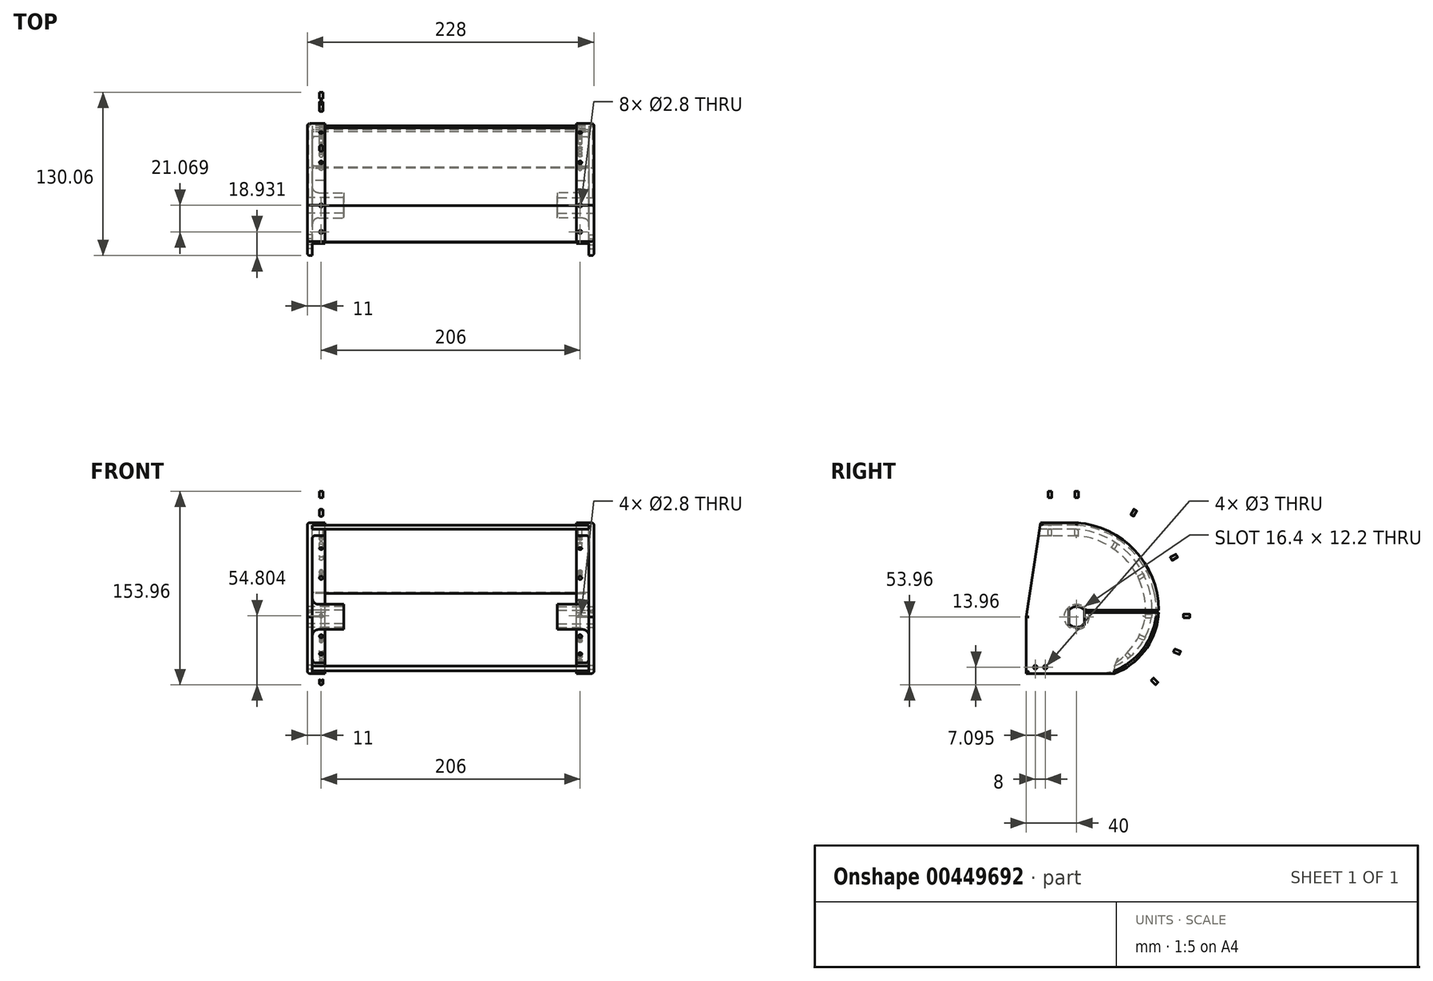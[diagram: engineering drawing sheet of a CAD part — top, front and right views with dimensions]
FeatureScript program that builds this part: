
annotation { "Feature Type Name" : "Feature", "Feature Type Description" : "" }
export const myFeature = defineFeature(function(context is Context, id is Id, definition is map)
    precondition{}
    {
        {
            var Q0;
            Q0=qCreatedBy(makeId("Right.planeOp"),FACE);
            var sketch = newSketch(context, id + "F0", { "sketchPlane" : qUnion([Q0])});
            skCircle(sketch, "E0", {"center": v(0, 0) * mm, "radius": 40 * mm});
            skCircle(sketch, "E1", {"center": v(0, 0) * mm, "radius": 8.2 * mm});
            skLineSegment(sketch, "E2", {"start": v(-6.1, 5.48) * mm, "end": v(-6.1, -5.48) * mm});
            skLineSegment(sketch, "E3", {"start": v(6.1, -5.48) * mm, "end": v(6.1, 5.48) * mm});
            skLineSegment(sketch, "E4", {"start": v(0, 0) * mm, "end": v(0, -45) * mm, "construction": true});
            skLineSegment(sketch, "E5", {"start": v(0, 0) * mm, "end": v(65, 0) * mm, "construction": true});
            skLineSegment(sketch, "E6", {"start": v(0, 0) * mm, "end": v(0, 75) * mm, "construction": true});
            skArc(sketch, "E7", {"start": v(65, 0) * mm, "mid": v(48.17, 51.08) * mm, "end": v(0, 75) * mm});
            skLineSegment(sketch, "E8", {"start": v(0, -45) * mm, "end": v(30, -45) * mm});
            skArc(sketch, "E9", {"start": v(30, -45) * mm, "mid": v(53.79, -27.4) * mm, "end": v(65, 0) * mm});
            skLineSegment(sketch, "E10", {"start": v(0, -45) * mm, "end": v(-40, -45) * mm});
            skLineSegment(sketch, "E11", {"start": v(-40, -45) * mm, "end": v(-40, 0) * mm});
            skLineSegment(sketch, "E12", {"start": v(-28.66, 75) * mm, "end": v(0, 75) * mm});
            skLineSegment(sketch, "E13", {"start": v(-40, 0) * mm, "end": v(-28.66, 75) * mm});
            skLineSegment(sketch, "E14.0", {"start": v(-28.96, 73) * mm, "end": v(-0.07, 73) * mm});
            skArc(sketch, "E14.1", {"start": v(61.76, 19.33) * mm, "mid": v(39.87, 56.56) * mm, "end": v(-0.07, 73) * mm});
            skArc(sketch, "E14.2", {"start": v(29.5, -43.05) * mm, "mid": v(57.45, -17.97) * mm, "end": v(61.76, 19.33) * mm});
            skArc(sketch, "E15.0", {"start": v(20.83, -42.2) * mm, "mid": v(52.6, -19.83) * mm, "end": v(58.54, 18.58) * mm});
            skArc(sketch, "E15.1", {"start": v(58.54, 18.58) * mm, "mid": v(37.77, 54) * mm, "end": v(-0.18, 69.7) * mm});
            skLineSegment(sketch, "E15.2", {"start": v(-29.46, 69.7) * mm, "end": v(-0.18, 69.7) * mm});
            skArc(sketch, "E16.1", {"start": v(54.69, 0.26) * mm, "mid": v(40.66, 44) * mm, "end": v(-0.35, 64.7) * mm});
            skLineSegment(sketch, "E16.2", {"start": v(-30.22, 64.7) * mm, "end": v(-0.35, 64.7) * mm});
            skLineSegment(sketch, "E17", {"start": v(29.5, -43.05) * mm, "end": v(19.71, -45) * mm});
            skLineSegment(sketch, "E18", {"start": v(20.86, -42.37) * mm, "end": v(20.83, -42.2) * mm});
            skArc(sketch, "E19", {"start": v(20.86, -42.37) * mm, "mid": v(43.09, -25.27) * mm, "end": v(54.69, 0.26) * mm});
            skLineSegment(sketch, "E20", {"start": v(30.2, -39.2) * mm, "end": v(31.32, -36.44) * mm});
            skPoint(sketch, "E21", {"position": v(-32.9, -40) * mm});
            skPoint(sketch, "E22", {"position": v(-24.9, -40) * mm});
            skCircle(sketch, "E23", {"center": v(-32.9, -40) * mm, "radius": 1.5 * mm});
            skCircle(sketch, "E24", {"center": v(-24.9, -40) * mm, "radius": 1.5 * mm});
            skSolve(sketch);
        }
        {
            var Q0;
            Q0=makeQuery(id+"F0.imprint","IMPRINT",FACE,{"disambiguationData":[TD([[makeQuery(id+"F0.imprint","IMPRINT",EDGE,{"derivedFrom":sQuery(id+"F0.wireOp",EDGE,"E7")}),1.0]])]});
            var Q1;
            {var subQ4=sQuery(id+"F0.wireOp",EDGE,"E1");var subQ8=sQuery(id+"F0.wireOp",EDGE,"E2");var subQ9=makeQuery(id+"F0.imprint","INTERSECT",VERTEX,{"disambiguationData":[OD(0.0)],"derivedFrom":[subQ4,subQ8]});Q1=makeQuery(id+"F0.imprint","IMPRINT",FACE,{"disambiguationData":[TD([[makeQuery(id+"F0.imprint","IMPRINT",EDGE,{"disambiguationData":[TD([[subQ9,1.0]])],"derivedFrom":subQ4}),-1.0]])]});}
            var Q2;
            {var subQ0=sQuery(id+"F0.wireOp",EDGE,"E2");Q2=makeQuery(id+"F0.imprint","IMPRINT",FACE,{"disambiguationData":[TD([[makeQuery(id+"F0.imprint","IMPRINT",EDGE,{"derivedFrom":subQ0}),-1.0]])]});}
            var Q3;
            {var subQ0=sQuery(id+"F0.wireOp",EDGE,"E3");Q3=makeQuery(id+"F0.imprint","IMPRINT",FACE,{"disambiguationData":[TD([[makeQuery(id+"F0.imprint","IMPRINT",EDGE,{"derivedFrom":subQ0}),-1.0]])]});}
            var Q4;
            {var subQ12=sQuery(id+"F0.wireOp",EDGE,"E10");Q4=makeQuery(id+"F0.imprint","IMPRINT",FACE,{"disambiguationData":[TD([[makeQuery(id+"F0.imprint","IMPRINT",EDGE,{"derivedFrom":subQ12}),-1.0]])]});}
            var Q5;
            {var subQ4=sQuery(id+"F0.wireOp",EDGE,"E15.0");Q5=makeQuery(id+"F0.imprint","IMPRINT",FACE,{"disambiguationData":[TD([[makeQuery(id+"F0.imprint","IMPRINT",EDGE,{"derivedFrom":subQ4}),1.0]])]});}
            var Q6;
            {var subQ4=sQuery(id+"F0.wireOp",EDGE,"E14.0");Q6=makeQuery(id+"F0.imprint","IMPRINT",FACE,{"disambiguationData":[TD([[makeQuery(id+"F0.imprint","IMPRINT",EDGE,{"derivedFrom":subQ4}),-1.0]])]});}
            var Q7;
            {var subQ0=sQuery(id+"F0.wireOp",EDGE,"E18");Q7=makeQuery(id+"F0.imprint","IMPRINT",FACE,{"disambiguationData":[TD([[makeQuery(id+"F0.imprint","IMPRINT",EDGE,{"derivedFrom":subQ0}),1.0]])]});}
            var Q8;
            {var subQ7=sQuery(id+"F0.wireOp",EDGE,"E15.1");Q8=makeQuery(id+"F0.imprint","IMPRINT",FACE,{"disambiguationData":[TD([[makeQuery(id+"F0.imprint","IMPRINT",EDGE,{"derivedFrom":subQ7}),1.0]])]});}
            var Q9;
            {var subQ0=sQuery(id+"F0.wireOp",EDGE,"E18");Q9=makeQuery(id+"F0.imprint","IMPRINT",FACE,{"disambiguationData":[TD([[makeQuery(id+"F0.imprint","IMPRINT",EDGE,{"derivedFrom":subQ0}),-1.0]])]});}
            var Q10;
            Q10=sQuery(id+"F0.wireOp",EDGE,"E12");
            var Q11;
            Q11=sQuery(id+"F0.wireOp",EDGE,"E13");
            var Q12;
            Q12=sQuery(id+"F0.wireOp",EDGE,"E11");
            var Q13;
            Q13=sQuery(id+"F0.wireOp",EDGE,"E10");
            var Q14;
            Q14=sQuery(id+"F0.wireOp",EDGE,"E8");
            var Q15;
            Q15=sQuery(id+"F0.wireOp",EDGE,"E9");
            var Q16;
            Q16=sQuery(id+"F0.wireOp",EDGE,"E7");
            extrude(context, id + "F1", {"entities" : qUnion([Q0, Q1, Q2, Q3, Q4, Q5, Q6, Q7, Q8, Q9]), "surfaceEntities" : qUnion([Q10, Q11, Q12, Q13, Q14, Q15, Q16]), "depth" : 29 * mm});
        }
        {
            var Q0;
            Q0=makeQuery(id+"F1.opExtrude","CAP_FACE",FACE,{"disambiguationData":[OSD([sQuery(id+"F0.wireOp",EDGE,"E1"),sQuery(id+"F0.wireOp",EDGE,"E2"),sQuery(id+"F0.wireOp",EDGE,"E3"),sQuery(id+"F0.wireOp",EDGE,"E7"),sQuery(id+"F0.wireOp",EDGE,"E8"),sQuery(id+"F0.wireOp",EDGE,"E9"),sQuery(id+"F0.wireOp",EDGE,"E10"),sQuery(id+"F0.wireOp",EDGE,"E11"),sQuery(id+"F0.wireOp",EDGE,"E12"),sQuery(id+"F0.wireOp",EDGE,"E13"),sQuery(id+"F0.wireOp",EDGE,"b91848d7-33e1-4d5c-aaae-2f8c404cd7a8"),sQuery(id+"F0.wireOp",EDGE,"291409aa-1abd-44d4-8dab-fd7a7754a467")])],"isStart":false});
            var sketch = newSketch(context, id + "F2", { "sketchPlane" : qUnion([Q0])});
            skCircle(sketch, "E25", {"center": v(0, 0) * mm, "radius": 10 * mm});
            skSolve(sketch);
        }
        {
            var Q0;
            {var subQ1=sQuery(id+"F0.wireOp",EDGE,"E2");Q0=makeQuery(id+"F2.imprint","IMPRINT",FACE,{"disambiguationData":[TD([[makeQuery(id+"F2.imprint","IMPRINT",EDGE,{"derivedFrom":makeQuery(id+"F1.opExtrude","CAP_EDGE",EDGE,{"disambiguationData":[OSD([subQ1])],"isStart":true})}),-1.0]])]});}
            var Q1;
            Q1=makeQuery(id+"F2.imprint","IMPRINT",FACE,{"disambiguationData":[TD([[makeQuery(id+"F2.imprint","IMPRINT",EDGE,{"derivedFrom":sQuery(id+"F2.wireOp",EDGE,"E25")}),-1.0]])]});
            extrude(context, id + "F3", {"entities" : qUnion([Q0, Q1]), "operationType" : NewBodyOperationType.REMOVE, "oppositeDirection" : true, "depth" : 25 * mm});
        }
        {
            var Q0;
            {var subQ7=sQuery(id+"F0.wireOp",EDGE,"E15.1");Q0=makeQuery(id+"F0.imprint","IMPRINT",FACE,{"disambiguationData":[TD([[makeQuery(id+"F0.imprint","IMPRINT",EDGE,{"derivedFrom":subQ7}),1.0]])]});}
            extrude(context, id + "F4", {"entities" : qUnion([Q0]), "operationType" : NewBodyOperationType.ADD, "depth" : 10 * mm});
        }
        {
            var Q0;
            Q0=makeQuery(id+"F0.imprint","IMPRINT",FACE,{"disambiguationData":[TD([[makeQuery(id+"F0.imprint","IMPRINT",EDGE,{"derivedFrom":sQuery(id+"F0.wireOp",EDGE,"E7")}),1.0]])]});
            extrude(context, id + "F5", {"entities" : qUnion([Q0]), "operationType" : NewBodyOperationType.ADD, "depth" : 10 * mm});
        }
        {
            var Q0;
            Q0=makeQuery(id+"F3.boolean.opBoolean","COPY",EDGE,{"derivedFrom":makeQuery(id+"F3.opExtrude","CAP_EDGE",EDGE,{"disambiguationData":[OSD([sQuery(id+"F2.wireOp",EDGE,"E25")])],"isStart":false})});
            fillet(context, id + "F6", {"entities" : qUnion([Q0]), "radius" : 5 * mm, "tangentPropagation" : true, "allowEdgeOverflow" : false});
        }
        {
            var Q0;
            Q0=makeQuery(id+"F3.boolean.opBoolean","COPY",EDGE,{"derivedFrom":makeQuery(id+"F3.opExtrude","CAP_EDGE",EDGE,{"disambiguationData":[OSD([sQuery(id+"F2.wireOp",EDGE,"E25")])],"isStart":true})});
            var Q1;
            Q1=makeQuery(id+"F4.boolean.opBoolean","INTERSECT",EDGE,{"derivedFrom":[makeQuery(id+"F3.boolean.opBoolean","COPY",FACE,{"derivedFrom":makeQuery(id+"F3.opExtrude","CAP_FACE",FACE,{"disambiguationData":[OSD([sQuery(id+"F0.wireOp",EDGE,"E7"),sQuery(id+"F0.wireOp",EDGE,"E8"),sQuery(id+"F0.wireOp",EDGE,"E9"),sQuery(id+"F0.wireOp",EDGE,"E10"),sQuery(id+"F0.wireOp",EDGE,"E11"),sQuery(id+"F0.wireOp",EDGE,"E12"),sQuery(id+"F0.wireOp",EDGE,"E13"),sQuery(id+"F2.wireOp",EDGE,"E25")])],"isStart":false})}),makeQuery(id+"F4.opExtrude","SWEPT_FACE",FACE,{"disambiguationData":[OSD([sQuery(id+"F0.wireOp",EDGE,"E19")])]})]});
            var Q2;
            Q2=makeQuery(id+"F4.boolean.opBoolean","INTERSECT",EDGE,{"derivedFrom":[makeQuery(id+"F3.boolean.opBoolean","COPY",FACE,{"derivedFrom":makeQuery(id+"F3.opExtrude","CAP_FACE",FACE,{"disambiguationData":[OSD([sQuery(id+"F0.wireOp",EDGE,"E7"),sQuery(id+"F0.wireOp",EDGE,"E8"),sQuery(id+"F0.wireOp",EDGE,"E9"),sQuery(id+"F0.wireOp",EDGE,"E10"),sQuery(id+"F0.wireOp",EDGE,"E11"),sQuery(id+"F0.wireOp",EDGE,"E12"),sQuery(id+"F0.wireOp",EDGE,"E13"),sQuery(id+"F2.wireOp",EDGE,"E25")])],"isStart":false})}),makeQuery(id+"F4.opExtrude","SWEPT_FACE",FACE,{"disambiguationData":[OSD([sQuery(id+"F0.wireOp",EDGE,"E16.1")])]})]});
            var Q3;
            Q3=makeQuery(id+"F4.boolean.opBoolean","INTERSECT",EDGE,{"derivedFrom":[makeQuery(id+"F3.boolean.opBoolean","COPY",FACE,{"derivedFrom":makeQuery(id+"F3.opExtrude","CAP_FACE",FACE,{"disambiguationData":[OSD([sQuery(id+"F0.wireOp",EDGE,"E7"),sQuery(id+"F0.wireOp",EDGE,"E8"),sQuery(id+"F0.wireOp",EDGE,"E9"),sQuery(id+"F0.wireOp",EDGE,"E10"),sQuery(id+"F0.wireOp",EDGE,"E11"),sQuery(id+"F0.wireOp",EDGE,"E12"),sQuery(id+"F0.wireOp",EDGE,"E13"),sQuery(id+"F2.wireOp",EDGE,"E25")])],"isStart":false})}),makeQuery(id+"F4.opExtrude","SWEPT_FACE",FACE,{"disambiguationData":[OSD([sQuery(id+"F0.wireOp",EDGE,"E16.2")])]})]});
            var Q4;
            {var subQ0=sQuery(id+"F0.wireOp",EDGE,"E13");var subQ1=sQuery(id+"F0.wireOp",EDGE,"E11");Q4=makeQuery(id+"F4.boolean.opBoolean","SPLIT",EDGE,{"disambiguationData":[TD([makeQuery(id+"F1.opExtrude","SWEPT_FACE",FACE,{"disambiguationData":[OSD([subQ1])]})])],"derivedFrom":makeQuery(id+"F3.boolean.opBoolean","COPY",EDGE,{"derivedFrom":makeQuery(id+"F3.opExtrude","CAP_EDGE",EDGE,{"disambiguationData":[OSD([subQ0])],"isStart":false})})});}
            var Q5;
            Q5=makeQuery(id+"F3.boolean.opBoolean","COPY",EDGE,{"derivedFrom":makeQuery(id+"F3.opExtrude","CAP_EDGE",EDGE,{"disambiguationData":[OSD([sQuery(id+"F0.wireOp",EDGE,"E11")])],"isStart":false})});
            var Q6;
            Q6=makeQuery(id+"F3.boolean.opBoolean","COPY",EDGE,{"derivedFrom":makeQuery(id+"F3.opExtrude","CAP_EDGE",EDGE,{"disambiguationData":[OSD([sQuery(id+"F0.wireOp",EDGE,"E8"),sQuery(id+"F0.wireOp",EDGE,"E10")])],"isStart":false})});
            var Q7;
            Q7=makeQuery(id+"F1.opExtrude","CAP_EDGE",EDGE,{"disambiguationData":[OSD([sQuery(id+"F0.wireOp",EDGE,"E11")])],"isStart":true});
            var Q8;
            Q8=makeQuery(id+"F1.opExtrude","CAP_EDGE",EDGE,{"disambiguationData":[OSD([sQuery(id+"F0.wireOp",EDGE,"E13")])],"isStart":true});
            var Q9;
            Q9=makeQuery(id+"F1.opExtrude","CAP_EDGE",EDGE,{"disambiguationData":[OSD([sQuery(id+"F0.wireOp",EDGE,"E8"),sQuery(id+"F0.wireOp",EDGE,"E10")])],"isStart":true});
            var Q10;
            Q10=makeQuery(id+"F1.opExtrude","CAP_EDGE",EDGE,{"disambiguationData":[OSD([sQuery(id+"F0.wireOp",EDGE,"E9")])],"isStart":true});
            var Q11;
            Q11=makeQuery(id+"F1.opExtrude","CAP_EDGE",EDGE,{"disambiguationData":[OSD([sQuery(id+"F0.wireOp",EDGE,"E7")])],"isStart":true});
            fillet(context, id + "F7", {"entities" : qUnion([Q0, Q1, Q2, Q3, Q4, Q5, Q6, Q7, Q8, Q9, Q10, Q11]), "radius" : 2 * mm, "tangentPropagation" : true, "allowEdgeOverflow" : false});
        }
        {
            var Q0;
            Q0=makeQuery(id+"F4.opExtrude","CAP_FACE",FACE,{"disambiguationData":[OSD([sQuery(id+"F0.wireOp",EDGE,"E13"),sQuery(id+"F0.wireOp",EDGE,"E15.0"),sQuery(id+"F0.wireOp",EDGE,"E15.1"),sQuery(id+"F0.wireOp",EDGE,"E15.2"),sQuery(id+"F0.wireOp",EDGE,"E16.1"),sQuery(id+"F0.wireOp",EDGE,"E16.2"),sQuery(id+"F0.wireOp",EDGE,"E19"),sQuery(id+"F0.wireOp",EDGE,"E20")])],"isStart":false});
            var Q1;
            Q1=makeQuery(id+"F5.opExtrude","CAP_FACE",FACE,{"disambiguationData":[OSD([sQuery(id+"F0.wireOp",EDGE,"E7"),sQuery(id+"F0.wireOp",EDGE,"E8"),sQuery(id+"F0.wireOp",EDGE,"E9"),sQuery(id+"F0.wireOp",EDGE,"E12"),sQuery(id+"F0.wireOp",EDGE,"E13"),sQuery(id+"F0.wireOp",EDGE,"E14.0"),sQuery(id+"F0.wireOp",EDGE,"E14.1"),sQuery(id+"F0.wireOp",EDGE,"E14.2"),sQuery(id+"F0.wireOp",EDGE,"E17")])],"isStart":false});
            extrude(context, id + "F8", {"entities" : qUnion([Q0, Q1]), "operationType" : NewBodyOperationType.ADD, "depth" : 4 * mm});
        }
        {
            var Q0;
            {var subQ0=sQuery(id+"F0.wireOp",EDGE,"E12");Q0=makeQuery(id+"F8.boolean.opBoolean","MERGE",FACE,{"derivedFrom":[makeQuery(id+"F5.boolean.opBoolean","MERGE",FACE,{"derivedFrom":[makeQuery(id+"F1.opExtrude","SWEPT_FACE",FACE,{"disambiguationData":[OSD([subQ0])]}),makeQuery(id+"F5.opExtrude","SWEPT_FACE",FACE,{"disambiguationData":[OSD([subQ0])]})]}),makeQuery(id+"F8.opExtrude","SWEPT_FACE",FACE,{"disambiguationData":[OSD([subQ0])]})]});}
            var sketch = newSketch(context, id + "F9", { "sketchPlane" : qUnion([Q0])});
            skCircle(sketch, "E26", {"center": v(11, 0) * mm, "radius": 1.4 * mm});
            skCircle(sketch, "E27", {"center": v(11, -21.07) * mm, "radius": 1.4 * mm});
            skSolve(sketch);
        }
        {
            var Q0;
            Q0=makeQuery(id+"F9.imprint","IMPRINT",FACE,{"disambiguationData":[TD([[makeQuery(id+"F9.imprint","IMPRINT",EDGE,{"derivedFrom":sQuery(id+"F9.wireOp",EDGE,"E27")}),-1.0]])]});
            cPlane(context, id + "F10", {"entities" : qUnion([Q0]), "cplaneType" : CPlaneType.OFFSET, "offset" : 20 * mm, "width" : 150 * mm, "height" : 150 * mm});
        }
        {
            var Q0;
            Q0=qCreatedBy(id+"F10.planeOp",FACE);
            var sketch = newSketch(context, id + "F11", { "sketchPlane" : qUnion([Q0])});
            skCircle(sketch, "E28.0", {"center": v(11, 0) * mm, "radius": 1.4 * mm});
            skCircle(sketch, "E29.0", {"center": v(11, -21.07) * mm, "radius": 1.4 * mm});
            skSolve(sketch);
        }
        {
            var Q0;
            Q0=makeQuery(id+"F11.imprint","IMPRINT",FACE,{"disambiguationData":[TD([[makeQuery(id+"F11.imprint","IMPRINT",EDGE,{"derivedFrom":sQuery(id+"F11.wireOp",EDGE,"E28.0")}),1.0]])]});
            var Q1;
            Q1=makeQuery(id+"F11.imprint","IMPRINT",FACE,{"disambiguationData":[TD([[makeQuery(id+"F11.imprint","IMPRINT",EDGE,{"derivedFrom":sQuery(id+"F11.wireOp",EDGE,"E29.0")}),1.0]])]});
            extrude(context, id + "F12", {"entities" : qUnion([Q0, Q1]), "depth" : 5 * mm});
        }
        {
            var Q0;
            Q0=makeQuery(id+"F12.opExtrude","SWEPT_BODY",BODY,{"disambiguationData":[OSD([sQuery(id+"F11.wireOp",EDGE,"E28.0")])]});
            var Q1;
            {var subQ0=sQuery(id+"F0.wireOp",EDGE,"E7");Q1=makeQuery(id+"F8.boolean.opBoolean","MERGE",FACE,{"derivedFrom":[makeQuery(id+"F5.boolean.opBoolean","MERGE",FACE,{"derivedFrom":[makeQuery(id+"F1.opExtrude","SWEPT_FACE",FACE,{"disambiguationData":[OSD([subQ0])]}),makeQuery(id+"F5.opExtrude","SWEPT_FACE",FACE,{"disambiguationData":[OSD([subQ0])]})]}),makeQuery(id+"F8.opExtrude","SWEPT_FACE",FACE,{"disambiguationData":[OSD([subQ0])]})]});}
            circularPattern(context, id + "F13", {"entities" : qUnion([Q0]), "axis" : qUnion([Q1]), "angle" : 30 * degree, "instanceCount" : round(4)});
        }
        {
            var Q0;
            Q0=makeQuery(id+"F13.opPattern","COPY",BODY,{"derivedFrom":makeQuery(id+"F12.opExtrude","SWEPT_BODY",BODY,{"disambiguationData":[OSD([sQuery(id+"F11.wireOp",EDGE,"E28.0")])]}),"instanceName":"3"});
            var Q1;
            {var subQ0=sQuery(id+"F0.wireOp",EDGE,"E9");Q1=makeQuery(id+"F5.boolean.opBoolean","MERGE",FACE,{"derivedFrom":[makeQuery(id+"F1.opExtrude","SWEPT_FACE",FACE,{"disambiguationData":[OSD([subQ0])]}),makeQuery(id+"F5.opExtrude","SWEPT_FACE",FACE,{"disambiguationData":[OSD([subQ0])]})]});}
            circularPattern(context, id + "F14", {"entities" : qUnion([Q0]), "axis" : qUnion([Q1]), "angle" : 22 * degree, "instanceCount" : round(3)});
        }
        {
            var Q0;
            Q0=makeQuery(id+"F12.opExtrude","CAP_FACE",FACE,{"disambiguationData":[OSD([sQuery(id+"F11.wireOp",EDGE,"E29.0")])],"isStart":true});
            var Q1;
            Q1=makeQuery(id+"F12.opExtrude","CAP_FACE",FACE,{"disambiguationData":[OSD([sQuery(id+"F11.wireOp",EDGE,"E28.0")])],"isStart":true});
            extrude(context, id + "F15", {"entities" : qUnion([Q0, Q1]), "operationType" : NewBodyOperationType.REMOVE, "depth" : 40 * mm});
        }
        {
            var Q0;
            Q0=makeQuery(id+"F13.opPattern","COPY",FACE,{"derivedFrom":makeQuery(id+"F12.opExtrude","CAP_FACE",FACE,{"disambiguationData":[OSD([sQuery(id+"F11.wireOp",EDGE,"E28.0")])],"isStart":true}),"instanceName":"1"});
            extrude(context, id + "F16", {"entities" : qUnion([Q0]), "operationType" : NewBodyOperationType.REMOVE, "depth" : 40 * mm});
        }
        {
            var Q0;
            Q0=makeQuery(id+"F13.opPattern","COPY",FACE,{"derivedFrom":makeQuery(id+"F12.opExtrude","CAP_FACE",FACE,{"disambiguationData":[OSD([sQuery(id+"F11.wireOp",EDGE,"E28.0")])],"isStart":true}),"instanceName":"2"});
            extrude(context, id + "F17", {"entities" : qUnion([Q0]), "operationType" : NewBodyOperationType.REMOVE, "depth" : 40 * mm});
        }
        {
            var Q0;
            Q0=makeQuery(id+"F13.opPattern","COPY",FACE,{"derivedFrom":makeQuery(id+"F12.opExtrude","CAP_FACE",FACE,{"disambiguationData":[OSD([sQuery(id+"F11.wireOp",EDGE,"E28.0")])],"isStart":true}),"instanceName":"3"});
            extrude(context, id + "F18", {"entities" : qUnion([Q0]), "operationType" : NewBodyOperationType.REMOVE, "depth" : 40 * mm});
        }
        {
            var Q0;
            Q0=makeQuery(id+"F14.opPattern","COPY",FACE,{"derivedFrom":makeQuery(id+"F13.opPattern","COPY",FACE,{"derivedFrom":makeQuery(id+"F12.opExtrude","CAP_FACE",FACE,{"disambiguationData":[OSD([sQuery(id+"F11.wireOp",EDGE,"E28.0")])],"isStart":true}),"instanceName":"3"}),"instanceName":"1"});
            extrude(context, id + "F19", {"entities" : qUnion([Q0]), "operationType" : NewBodyOperationType.REMOVE, "depth" : 40 * mm});
        }
        {
            var Q0;
            Q0=makeQuery(id+"F14.opPattern","COPY",FACE,{"derivedFrom":makeQuery(id+"F13.opPattern","COPY",FACE,{"derivedFrom":makeQuery(id+"F12.opExtrude","CAP_FACE",FACE,{"disambiguationData":[OSD([sQuery(id+"F11.wireOp",EDGE,"E28.0")])],"isStart":true}),"instanceName":"3"}),"instanceName":"2"});
            extrude(context, id + "F20", {"entities" : qUnion([Q0]), "operationType" : NewBodyOperationType.REMOVE, "depth" : 40 * mm});
        }
        {
            var Q0;
            Q0=makeQuery(id+"F1.opExtrude","CAP_EDGE",EDGE,{"disambiguationData":[OSD([sQuery(id+"F0.wireOp",EDGE,"E3")])],"isStart":true});
            var Q1;
            {var subQ0=sQuery(id+"F0.wireOp",EDGE,"E1");Q1=makeQuery(id+"F1.opExtrude","CAP_EDGE",EDGE,{"disambiguationData":[OSD([subQ0]),TDD([makeQuery(id+"F0.imprint","IMPRINT",EDGE,{"disambiguationData":[TD([[makeQuery(id+"F0.imprint","INTERSECT",VERTEX,{"disambiguationData":[OD(0.0)],"derivedFrom":[subQ0,sQuery(id+"F0.wireOp",EDGE,"E2")]}),1.0]])],"derivedFrom":subQ0})])],"isStart":true});}
            var Q2;
            Q2=makeQuery(id+"F1.opExtrude","CAP_EDGE",EDGE,{"disambiguationData":[OSD([sQuery(id+"F0.wireOp",EDGE,"E2")])],"isStart":true});
            var Q3;
            {var subQ0=sQuery(id+"F0.wireOp",EDGE,"E1");Q3=makeQuery(id+"F1.opExtrude","CAP_EDGE",EDGE,{"disambiguationData":[OSD([subQ0]),TDD([makeQuery(id+"F0.imprint","IMPRINT",EDGE,{"disambiguationData":[TD([[makeQuery(id+"F0.imprint","INTERSECT",VERTEX,{"disambiguationData":[OD(1.0)],"derivedFrom":[subQ0,sQuery(id+"F0.wireOp",EDGE,"E2")]}),-1.0]])],"derivedFrom":subQ0})])],"isStart":true});}
            fillet(context, id + "F21", {"entities" : qUnion([Q0, Q1, Q2, Q3]), "radius" : 1 * mm, "tangentPropagation" : true, "allowEdgeOverflow" : false});
        }
        {
            var Q0;
            Q0=makeQuery(id+"F1.opExtrude","CAP_FACE",FACE,{"disambiguationData":[OSD([sQuery(id+"F0.wireOp",EDGE,"E1"),sQuery(id+"F0.wireOp",EDGE,"E2"),sQuery(id+"F0.wireOp",EDGE,"E3"),sQuery(id+"F0.wireOp",EDGE,"E7"),sQuery(id+"F0.wireOp",EDGE,"E8"),sQuery(id+"F0.wireOp",EDGE,"E9"),sQuery(id+"F0.wireOp",EDGE,"E10"),sQuery(id+"F0.wireOp",EDGE,"E11"),sQuery(id+"F0.wireOp",EDGE,"E12"),sQuery(id+"F0.wireOp",EDGE,"E13"),sQuery(id+"F0.wireOp",EDGE,"E23"),sQuery(id+"F0.wireOp",EDGE,"E24")])],"isStart":true});
            var sketch = newSketch(context, id + "F22", { "sketchPlane" : qUnion([Q0])});
            skCircle(sketch, "E30", {"center": v(-65.2, 4.44) * mm, "radius": 1 * mm});
            skArc(sketch, "E31.0", {"start": v(-30, -45) * mm, "mid": v(-53.79, -27.4) * mm, "end": v(-65, 0) * mm});
            skArc(sketch, "E32.0", {"start": v(-65, 0) * mm, "mid": v(-48.17, 51.08) * mm, "end": v(0, 75) * mm});
            skLineSegment(sketch, "E33", {"start": v(-65.2, 4.44) * mm, "end": v(-3.8, 4.44) * mm});
            skCircle(sketch, "E34", {"center": v(-65.2, 4.44) * mm, "radius": 1.5 * mm});
            skLineSegment(sketch, "E35", {"start": v(-65.6, 5.36) * mm, "end": v(-65.84, 5.81) * mm});
            skSolve(sketch);
        }
        {
            var Q0;
            {var subQ0=sQuery(id+"F22.wireOp",EDGE,"E33");var subQ1=sQuery(id+"F22.wireOp",EDGE,"E30");var subQ2=makeQuery(id+"F22.imprint","INTERSECT",VERTEX,{"derivedFrom":[subQ1,subQ0]});Q0=makeQuery(id+"F22.imprint","IMPRINT",FACE,{"disambiguationData":[TD([[makeQuery(id+"F22.imprint","IMPRINT",EDGE,{"disambiguationData":[TD([[subQ2,1.0]])],"derivedFrom":subQ1}),1.0]])]});}
            var Q1;
            {var subQ0=sQuery(id+"F22.wireOp",EDGE,"E32.0");var subQ1=sQuery(id+"F22.wireOp",EDGE,"E30");var subQ2=makeQuery(id+"F22.imprint","INTERSECT",VERTEX,{"disambiguationData":[OD(0.0)],"derivedFrom":[subQ1,subQ0]});Q1=makeQuery(id+"F22.imprint","IMPRINT",FACE,{"disambiguationData":[TD([[makeQuery(id+"F22.imprint","IMPRINT",EDGE,{"disambiguationData":[TD([[subQ2,1.0]])],"derivedFrom":subQ1}),1.0]])]});}
            extrude(context, id + "F23", {"entities" : qUnion([Q0, Q1]), "operationType" : NewBodyOperationType.REMOVE, "oppositeDirection" : true, "depth" : 25 * mm});
        }
        {
            var Q0;
            Q0=qCreatedBy(makeId("Front.planeOp"),FACE);
            cPlane(context, id + "F24", {"entities" : qUnion([Q0]), "cplaneType" : CPlaneType.OFFSET, "offset" : 65 * mm, "oppositeDirection" : true, "width" : 150 * mm, "height" : 150 * mm});
        }
        {
            var Q0;
            Q0=qCreatedBy(id+"F24.planeOp",FACE);
            var sketch = newSketch(context, id + "F25", { "sketchPlane" : qUnion([Q0])});
            skFitSpline(sketch, "E36.0", {"points": [v(2, 3.44) * mm, v(1.7, 3.44) * mm, v(1.48, 3.45) * mm, v(1.36, 3.45) * mm, v(1.25, 3.46) * mm, v(1.15, 3.47) * mm, v(1.07, 3.48) * mm, v(0.96, 3.5) * mm, v(0.87, 3.51) * mm, v(0.8, 3.54) * mm, v(0.7, 3.57) * mm, v(0.61, 3.62) * mm, v(0.54, 3.68) * mm, v(0.47, 3.75) * mm, v(0.4, 3.83) * mm, v(0.36, 3.93) * mm, v(0.33, 4) * mm, v(0.3, 4.09) * mm, v(0.3, 4.18) * mm, v(0.28, 4.27) * mm, v(0.27, 4.36) * mm, v(0.27, 4.45) * mm, v(0.27, 4.57) * mm, v(0.28, 4.67) * mm, v(0.3, 4.77) * mm, v(0.32, 4.88) * mm, v(0.35, 4.97) * mm, v(0.4, 5.05) * mm, v(0.44, 5.13) * mm, v(0.5, 5.2) * mm, v(0.57, 5.24) * mm, v(0.63, 5.3) * mm, v(0.7, 5.33) * mm, v(0.8, 5.36) * mm, v(0.87, 5.39) * mm, v(0.96, 5.4) * mm, v(1.06, 5.42) * mm, v(1.15, 5.43) * mm, v(1.24, 5.44) * mm, v(1.36, 5.44) * mm, v(1.44, 5.44) * mm, v(1.55, 5.44) * mm, v(1.68, 5.44) * mm, v(1.71, 5.44) * mm, v(1.82, 5.44) * mm, v(2, 5.44) * mm]});
            skLineSegment(sketch, "E37.0", {"start": v(0, 0.2) * mm, "end": v(0, 73) * mm});
            skLineSegment(sketch, "E38", {"start": v(0.27, 4.45) * mm, "end": v(0, 4.45) * mm});
            skCircle(sketch, "E39", {"center": v(0, 4.45) * mm, "radius": 1 * mm});
            skSolve(sketch);
        }
        {
            var Q0;
            {var subQ0=sQuery(id+"F25.wireOp",EDGE,"E38");Q0=makeQuery(id+"F25.imprint","IMPRINT",FACE,{"disambiguationData":[TD([[makeQuery(id+"F25.imprint","IMPRINT",EDGE,{"derivedFrom":subQ0}),1.0]])]});}
            var Q1;
            {var subQ0=sQuery(id+"F25.wireOp",EDGE,"E36.0");var subQ3=makeQuery(id+"F25.imprint","INTERSECT",VERTEX,{"derivedFrom":[subQ0,sQuery(id+"F25.wireOp",EDGE,"E38")]});Q1=makeQuery(id+"F25.imprint","IMPRINT",FACE,{"disambiguationData":[TD([[makeQuery(id+"F25.imprint","IMPRINT",EDGE,{"disambiguationData":[TD([[subQ3,1.0]])],"derivedFrom":subQ0}),-1.0]])]});}
            var Q2;
            {var subQ5=sQuery(id+"F25.wireOp",EDGE,"E38");Q2=makeQuery(id+"F25.imprint","IMPRINT",FACE,{"disambiguationData":[TD([[makeQuery(id+"F25.imprint","IMPRINT",EDGE,{"derivedFrom":subQ5}),-1.0]])]});}
            var Q3;
            Q3=qCreatedBy(makeId("Front.planeOp"),FACE);
            extrude(context, id + "F26", {"entities" : qUnion([Q0, Q1, Q2]), "operationType" : NewBodyOperationType.REMOVE, "endBound" : BoundingType.UP_TO_SURFACE, "endBoundEntityFace" : qUnion([Q3]), "depth" : 25 * mm});
        }
        {
            var Q0;
            Q0=makeQuery(id+"F26.boolean.opBoolean","INTERSECT",EDGE,{"derivedFrom":[makeQuery(id+"F23.boolean.opBoolean","COPY",FACE,{"derivedFrom":makeQuery(id+"F23.opExtrude","SWEPT_FACE",FACE,{"disambiguationData":[OSD([sQuery(id+"F22.wireOp",EDGE,"E30")])]})}),makeQuery(id+"F26.opExtrude","SWEPT_FACE",FACE,{"disambiguationData":[OSD([sQuery(id+"F25.wireOp",EDGE,"E39")])]})]});
            fillet(context, id + "F27", {"entities" : qUnion([Q0]), "radius" : 2 * mm, "tangentPropagation" : true, "allowEdgeOverflow" : false});
        }
        {
            var Q0;
            Q0=makeQuery(id+"F3.boolean.opBoolean","COPY",FACE,{"derivedFrom":makeQuery(id+"F3.opExtrude","CAP_FACE",FACE,{"disambiguationData":[OSD([sQuery(id+"F0.wireOp",EDGE,"E7"),sQuery(id+"F0.wireOp",EDGE,"E8"),sQuery(id+"F0.wireOp",EDGE,"E9"),sQuery(id+"F0.wireOp",EDGE,"E10"),sQuery(id+"F0.wireOp",EDGE,"E11"),sQuery(id+"F0.wireOp",EDGE,"E12"),sQuery(id+"F0.wireOp",EDGE,"E13"),sQuery(id+"F0.wireOp",EDGE,"E23"),sQuery(id+"F0.wireOp",EDGE,"E24"),sQuery(id+"F2.wireOp",EDGE,"E25")])],"isStart":false})});
            var sketch = newSketch(context, id + "F28", { "sketchPlane" : qUnion([Q0])});
            skLineSegment(sketch, "E40", {"start": v(30.2, -39.2) * mm, "end": v(29.63, -43) * mm});
            skSolve(sketch);
        }
        {
            var Q0;
            Q0=makeQuery(id+"F28.imprint","IMPRINT",FACE,{"disambiguationData":[TD([[makeQuery(id+"F28.imprint","IMPRINT",EDGE,{"derivedFrom":sQuery(id+"F28.wireOp",EDGE,"E40")}),1.0]])]});
            extrude(context, id + "F29", {"entities" : qUnion([Q0]), "depth" : 220 * mm});
        }
        {
            var Q0;
            Q0=makeQuery(id+"F29.opExtrude","CAP_FACE",FACE,{"disambiguationData":[OSD([sQuery(id+"F0.wireOp",EDGE,"E7"),sQuery(id+"F0.wireOp",EDGE,"E8"),sQuery(id+"F0.wireOp",EDGE,"E9"),sQuery(id+"F0.wireOp",EDGE,"E10"),sQuery(id+"F0.wireOp",EDGE,"E11"),sQuery(id+"F0.wireOp",EDGE,"E12"),sQuery(id+"F0.wireOp",EDGE,"E13"),sQuery(id+"F0.wireOp",EDGE,"E14.0"),sQuery(id+"F0.wireOp",EDGE,"E14.1"),sQuery(id+"F0.wireOp",EDGE,"E14.2"),sQuery(id+"F0.wireOp",EDGE,"E15.0"),sQuery(id+"F0.wireOp",EDGE,"E15.1"),sQuery(id+"F0.wireOp",EDGE,"E15.2"),sQuery(id+"F0.wireOp",EDGE,"E23"),sQuery(id+"F0.wireOp",EDGE,"E24"),sQuery(id+"F2.wireOp",EDGE,"E25"),sQuery(id+"F28.wireOp",EDGE,"E40")])],"isStart":false});
            var Q1;
            Q1=makeQuery(id+"F29.opExtrude","CAP_VERTEX",VERTEX,{"disambiguationData":[OSD([sQuery(id+"F0.wireOp",EDGE,"E7"),sQuery(id+"F0.wireOp",EDGE,"E8"),sQuery(id+"F0.wireOp",EDGE,"E9"),sQuery(id+"F0.wireOp",EDGE,"E10"),sQuery(id+"F0.wireOp",EDGE,"E11"),sQuery(id+"F0.wireOp",EDGE,"E12"),sQuery(id+"F0.wireOp",EDGE,"E13"),sQuery(id+"F0.wireOp",EDGE,"E15.0"),sQuery(id+"F0.wireOp",EDGE,"E15.1"),sQuery(id+"F0.wireOp",EDGE,"E23"),sQuery(id+"F0.wireOp",EDGE,"E24"),sQuery(id+"F2.wireOp",EDGE,"E25")])],"isStart":false});
            cPlane(context, id + "F30", {"entities" : qUnion([Q0, Q1]), "cplaneType" : CPlaneType.PLANE_POINT, "offset" : 150 * mm, "width" : 150 * mm, "height" : 150 * mm});
        }
        {
            var Q0;
            Q0=qCreatedBy(id+"F30.planeOp",FACE);
            var Q1;
            Q1=makeQuery(id+"F3.boolean.opBoolean","COPY",FACE,{"derivedFrom":makeQuery(id+"F3.opExtrude","CAP_FACE",FACE,{"disambiguationData":[OSD([sQuery(id+"F0.wireOp",EDGE,"E7"),sQuery(id+"F0.wireOp",EDGE,"E8"),sQuery(id+"F0.wireOp",EDGE,"E9"),sQuery(id+"F0.wireOp",EDGE,"E10"),sQuery(id+"F0.wireOp",EDGE,"E11"),sQuery(id+"F0.wireOp",EDGE,"E12"),sQuery(id+"F0.wireOp",EDGE,"E13"),sQuery(id+"F0.wireOp",EDGE,"E23"),sQuery(id+"F0.wireOp",EDGE,"E24"),sQuery(id+"F2.wireOp",EDGE,"E25")])],"isStart":false})});
            cPlane(context, id + "F31", {"entities" : qUnion([Q0, Q1]), "cplaneType" : CPlaneType.MID_PLANE, "offset" : 150 * mm, "width" : 150 * mm, "height" : 150 * mm});
        }
        {
            var Q0;
            Q0=makeQuery(id+"F1.opExtrude","SWEPT_BODY",BODY,{"disambiguationData":[OSD([sQuery(id+"F0.wireOp",EDGE,"E1"),sQuery(id+"F0.wireOp",EDGE,"E2"),sQuery(id+"F0.wireOp",EDGE,"E3"),sQuery(id+"F0.wireOp",EDGE,"E7"),sQuery(id+"F0.wireOp",EDGE,"E8"),sQuery(id+"F0.wireOp",EDGE,"E9"),sQuery(id+"F0.wireOp",EDGE,"E10"),sQuery(id+"F0.wireOp",EDGE,"E11"),sQuery(id+"F0.wireOp",EDGE,"E12"),sQuery(id+"F0.wireOp",EDGE,"E13"),sQuery(id+"F0.wireOp",EDGE,"E23"),sQuery(id+"F0.wireOp",EDGE,"E24")])]});
            var Q1;
            Q1=qCreatedBy(id+"F31.planeOp",FACE);
            mirror(context, id + "F32", {"entities" : qUnion([Q0]), "mirrorPlane" : qUnion([Q1])});
        }
    });
